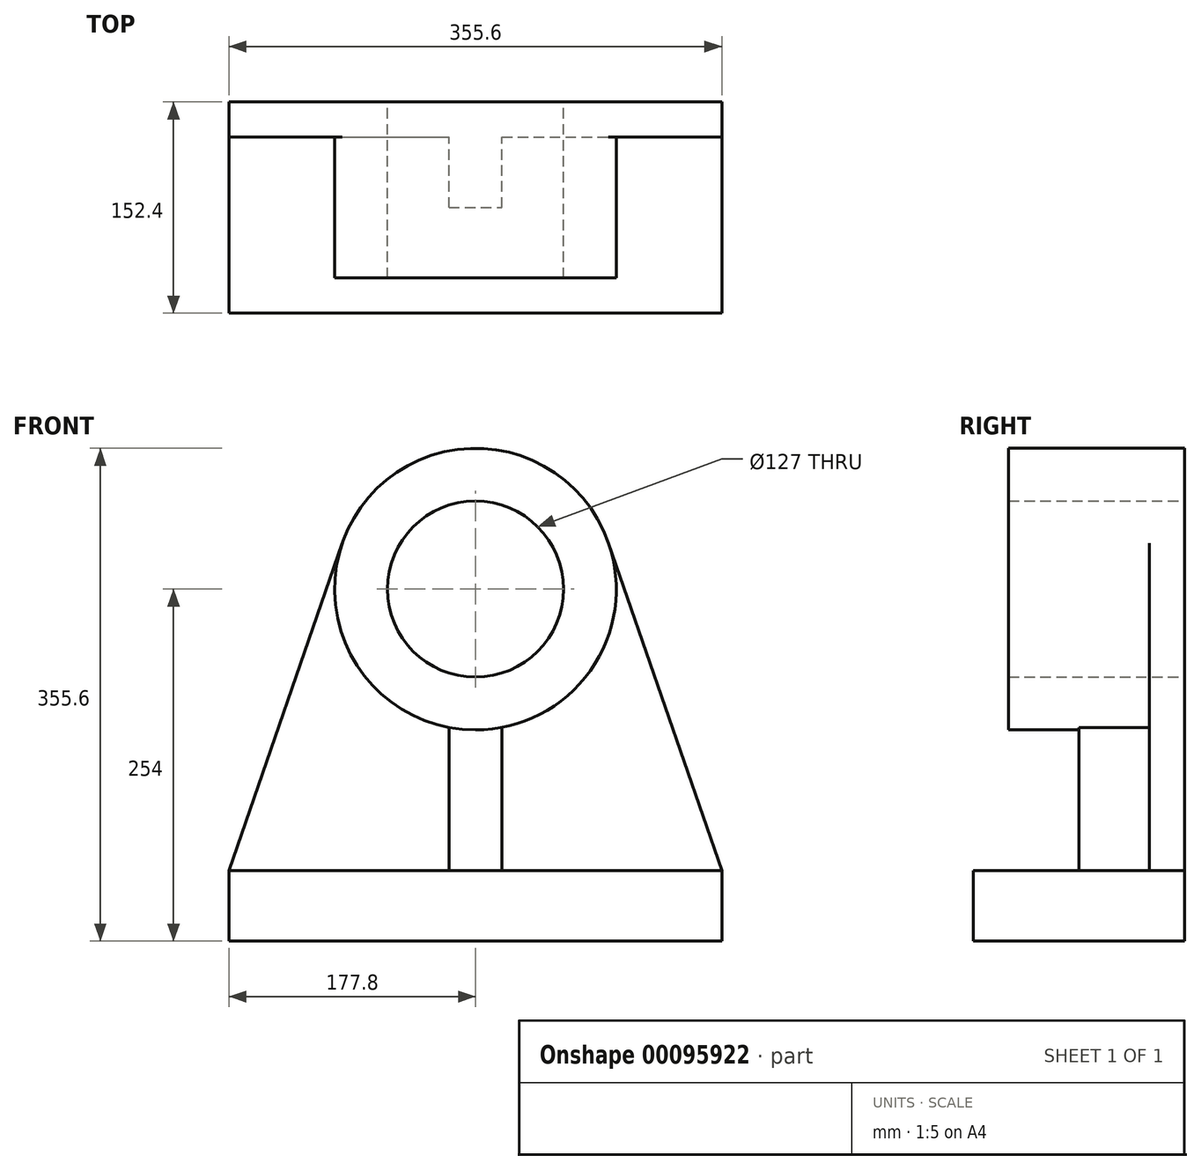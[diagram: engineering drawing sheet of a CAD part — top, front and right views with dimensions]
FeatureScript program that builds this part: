
annotation { "Feature Type Name" : "Feature", "Feature Type Description" : "" }
export const myFeature = defineFeature(function(context is Context, id is Id, definition is map)
    precondition{}
    {
        {
            var Q0;
            Q0=qCreatedBy(makeId("Front.planeOp"),FACE);
            var sketch = newSketch(context, id + "F0", { "sketchPlane" : qUnion([Q0])});
            skCircle(sketch, "E0", {"center": v(0, 0) * mm, "radius": 101.6 * mm});
            skCircle(sketch, "E1", {"center": v(0, 0) * mm, "radius": 63.5 * mm});
            skLineSegment(sketch, "E2", {"start": v(-177.8, -203.2) * mm, "end": v(177.8, -203.2) * mm});
            skLineSegment(sketch, "E3", {"start": v(-177.8, -203.2) * mm, "end": v(-177.8, -254) * mm});
            skLineSegment(sketch, "E4", {"start": v(177.8, -203.2) * mm, "end": v(177.8, -254) * mm});
            skLineSegment(sketch, "E5", {"start": v(177.8, -254) * mm, "end": v(-177.8, -254) * mm});
            skLineSegment(sketch, "E6", {"start": v(-19.05, -99.8) * mm, "end": v(-19.05, -203.2) * mm});
            skLineSegment(sketch, "E7", {"start": v(19.05, -99.8) * mm, "end": v(19.05, -203.2) * mm});
            skLineSegment(sketch, "E8", {"start": v(-96.02, 33.22) * mm, "end": v(-177.8, -203.2) * mm});
            skLineSegment(sketch, "E9", {"start": v(96.02, 33.22) * mm, "end": v(177.8, -203.2) * mm});
            skSolve(sketch);
        }
        {
            var Q0;
            Q0=makeQuery(id+"F0.imprint","IMPRINT",FACE,{"disambiguationData":[TD([[makeQuery(id+"F0.imprint","IMPRINT",EDGE,{"derivedFrom":sQuery(id+"F0.wireOp",EDGE,"E1")}),-1.0]])]});
            extrude(context, id + "F1", {"entities" : qUnion([Q0]), "depth" : 127 * mm});
        }
        {
            var Q0;
            {var subQ0=sQuery(id+"F0.wireOp",EDGE,"E3");Q0=makeQuery(id+"F0.imprint","IMPRINT",FACE,{"disambiguationData":[TD([[makeQuery(id+"F0.imprint","IMPRINT",EDGE,{"derivedFrom":subQ0}),1.0]])]});}
            extrude(context, id + "F2", {"entities" : qUnion([Q0]), "operationType" : NewBodyOperationType.ADD, "depth" : 152.4 * mm});
        }
        {
            var Q0;
            {var subQ0=sQuery(id+"F0.wireOp",EDGE,"E6");Q0=makeQuery(id+"F0.imprint","IMPRINT",FACE,{"disambiguationData":[TD([[makeQuery(id+"F0.imprint","IMPRINT",EDGE,{"derivedFrom":subQ0}),1.0]])]});}
            extrude(context, id + "F3", {"entities" : qUnion([Q0]), "operationType" : NewBodyOperationType.ADD, "depth" : 76.2 * mm});
        }
        {
            var Q0;
            {var subQ0=sQuery(id+"F0.wireOp",EDGE,"E6");Q0=makeQuery(id+"F0.imprint","IMPRINT",FACE,{"disambiguationData":[TD([[makeQuery(id+"F0.imprint","IMPRINT",EDGE,{"derivedFrom":subQ0}),-1.0]])]});}
            var Q1;
            {var subQ0=sQuery(id+"F0.wireOp",EDGE,"E7");Q1=makeQuery(id+"F0.imprint","IMPRINT",FACE,{"disambiguationData":[TD([[makeQuery(id+"F0.imprint","IMPRINT",EDGE,{"derivedFrom":subQ0}),1.0]])]});}
            extrude(context, id + "F4", {"entities" : qUnion([Q0, Q1]), "operationType" : NewBodyOperationType.ADD, "depth" : 25.4 * mm});
        }
    });
